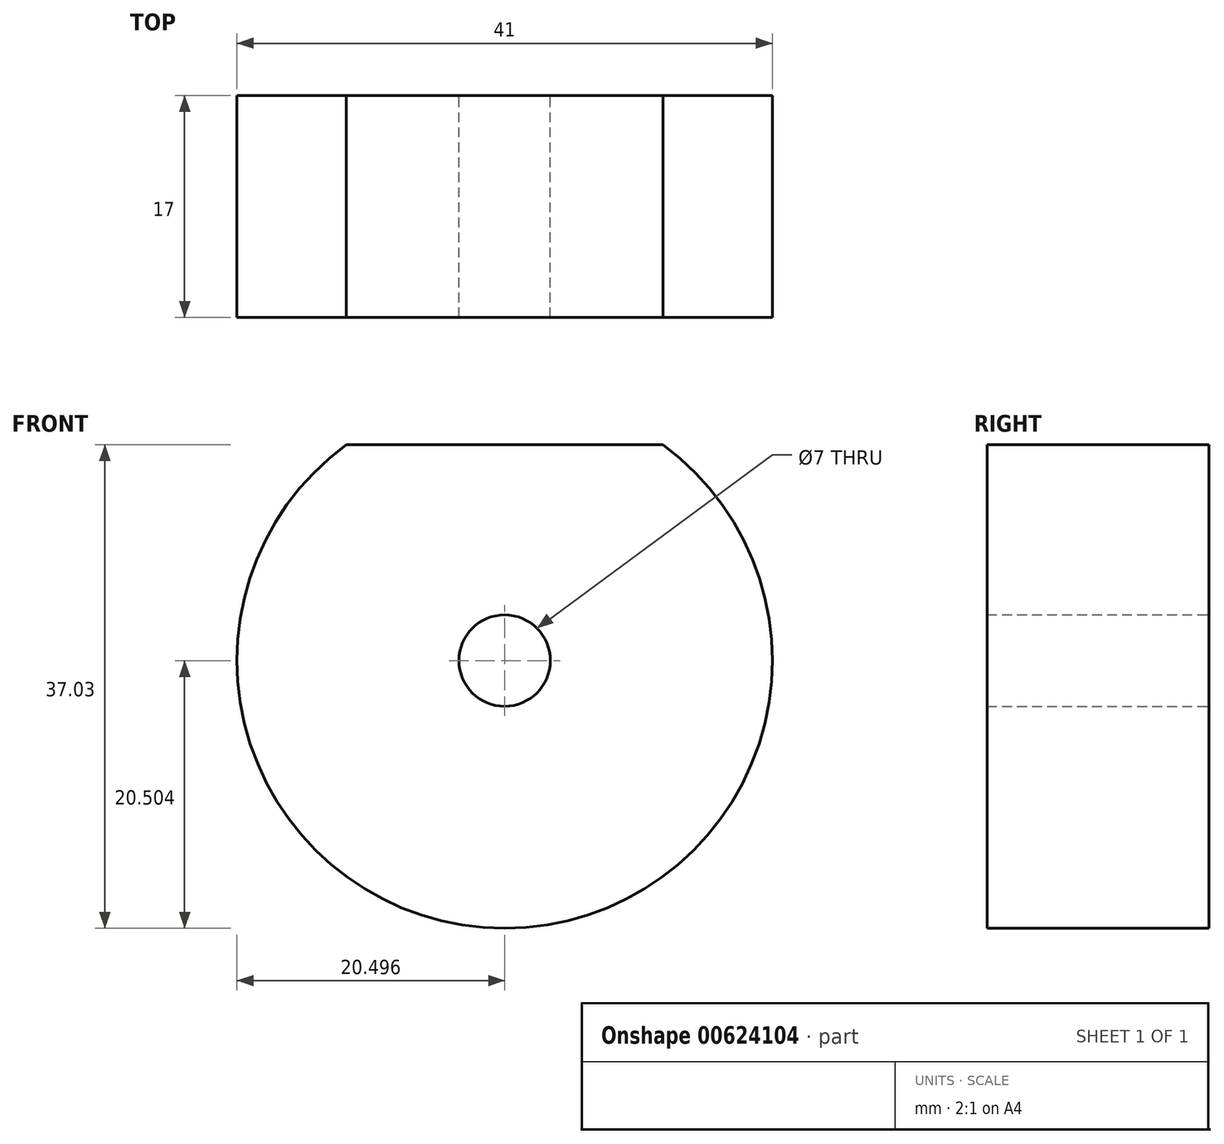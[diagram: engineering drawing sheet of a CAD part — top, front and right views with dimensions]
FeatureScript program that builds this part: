
annotation { "Feature Type Name" : "Feature", "Feature Type Description" : "" }
export const myFeature = defineFeature(function(context is Context, id is Id, definition is map)
    precondition{}
    {
        {
            var Q0;
            Q0=qCreatedBy(makeId("Front.planeOp"),FACE);
            var sketch = newSketch(context, id + "F0", { "sketchPlane" : qUnion([Q0])});
            skCircle(sketch, "E0", {"center": v(-19.87, 15.66) * mm, "radius": 20.5 * mm});
            skCircle(sketch, "E1", {"center": v(-19.87, 15.66) * mm, "radius": 3.5 * mm});
            skLineSegment(sketch, "E2", {"start": v(-18.92, -4.81) * mm, "end": v(50.8, -4.81) * mm, "construction": true});
            skLineSegment(sketch, "E3", {"start": v(50.8, -4.81) * mm, "end": v(50.8, 32.19) * mm, "construction": true});
            skLineSegment(sketch, "E4", {"start": v(-7.74, 32.19) * mm, "end": v(-32, 32.19) * mm});
            skSolve(sketch);
        }
        {
            var Q0;
            Q0=makeQuery(id+"F0.imprint","IMPRINT",FACE,{"disambiguationData":[TD([[makeQuery(id+"F0.imprint","IMPRINT",EDGE,{"derivedFrom":sQuery(id+"F0.wireOp",EDGE,"E1")}),-1.0]])]});
            extrude(context, id + "F1", {"entities" : qUnion([Q0]), "depth" : 17 * mm, "offsetDistance" : 25 * mm});
        }
    });
